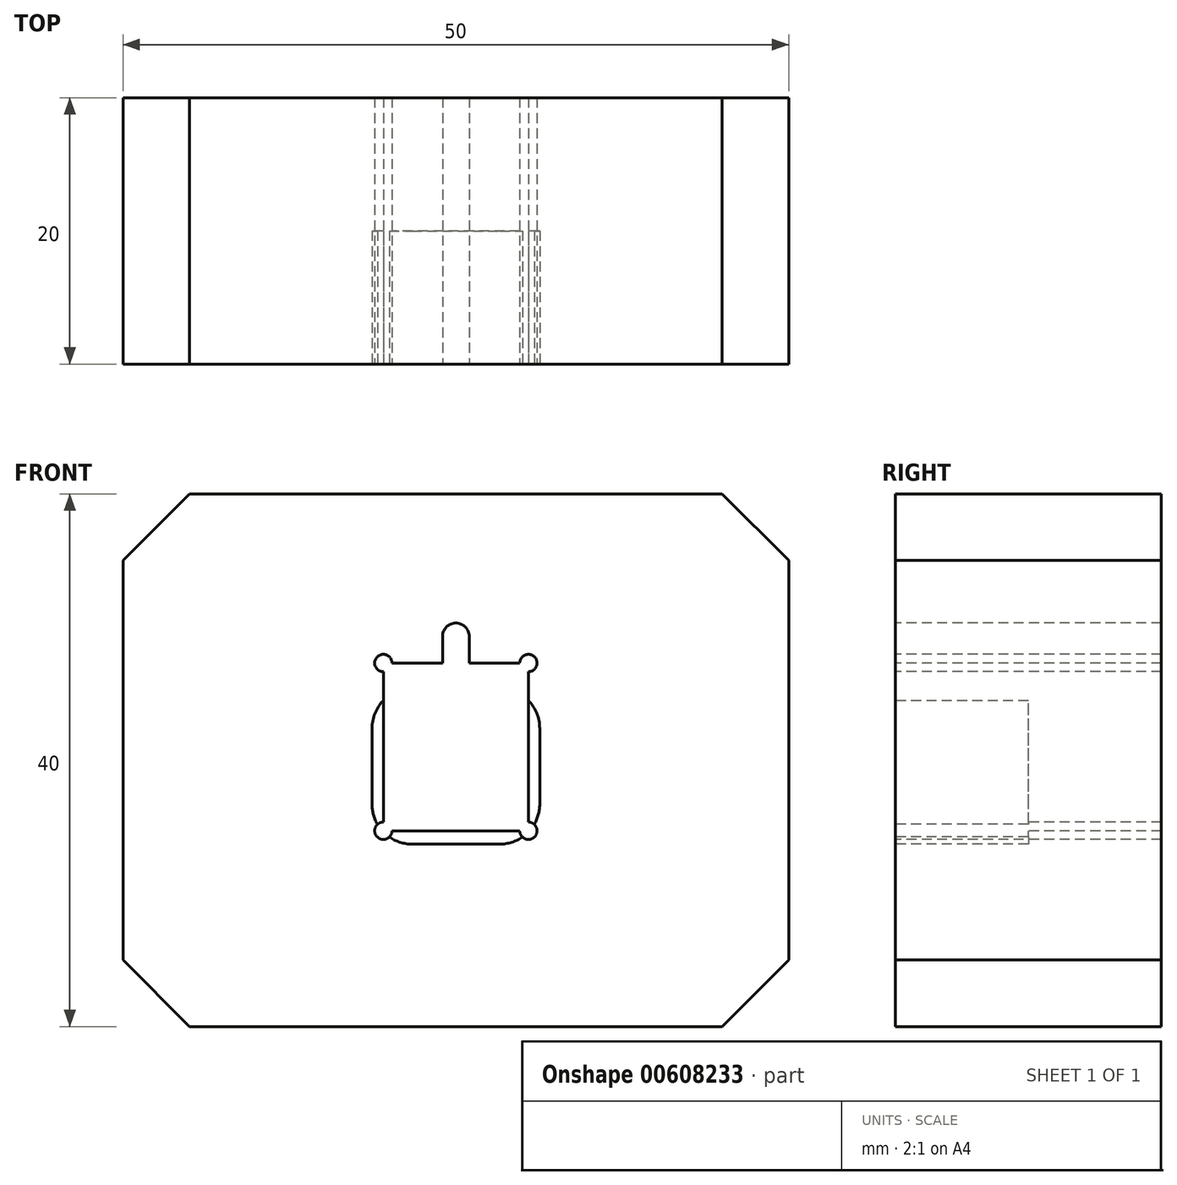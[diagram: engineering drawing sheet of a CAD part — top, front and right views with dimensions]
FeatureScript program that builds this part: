
annotation { "Feature Type Name" : "Feature", "Feature Type Description" : "" }
export const myFeature = defineFeature(function(context is Context, id is Id, definition is map)
    precondition{}
    {
        {
            var Q0;
            Q0=qCreatedBy(makeId("Front.planeOp"),FACE);
            var sketch = newSketch(context, id + "F0", { "sketchPlane" : qUnion([Q0])});
            skLineSegment(sketch, "E0.bottom", {"start": v(-25, 20) * mm, "end": v(25, 20) * mm});
            skLineSegment(sketch, "E0.top", {"start": v(-25, -20) * mm, "end": v(25, -20) * mm});
            skLineSegment(sketch, "E0.left", {"start": v(-25, 20) * mm, "end": v(-25, -20) * mm});
            skLineSegment(sketch, "E0.right", {"start": v(25, 20) * mm, "end": v(25, -20) * mm});
            skPoint(sketch, "E0.middle", {"position": v(0, 0) * mm});
            skSolve(sketch);
        }
        {
            var Q0;
            Q0 = qSketchRegion(id + "F0", true);
            extrude(context, id + "F1", {"entities" : qUnion([Q0]), "depth" : 20 * mm, "offsetDistance" : 25 * mm});
        }
        {
            var Q0;
            Q0=makeQuery(id+"F1.opExtrude","SWEPT_EDGE",EDGE,{"disambiguationData":[OSD([sQuery(id+"F0.wireOp",EDGE,"E0.bottom"),sQuery(id+"F0.wireOp",EDGE,"E0.left")])]});
            var Q1;
            Q1=makeQuery(id+"F1.opExtrude","SWEPT_EDGE",EDGE,{"disambiguationData":[OSD([sQuery(id+"F0.wireOp",EDGE,"E0.bottom"),sQuery(id+"F0.wireOp",EDGE,"E0.right")])]});
            var Q2;
            Q2=makeQuery(id+"F1.opExtrude","SWEPT_EDGE",EDGE,{"disambiguationData":[OSD([sQuery(id+"F0.wireOp",EDGE,"E0.top"),sQuery(id+"F0.wireOp",EDGE,"E0.left")])]});
            var Q3;
            Q3=makeQuery(id+"F1.opExtrude","SWEPT_EDGE",EDGE,{"disambiguationData":[OSD([sQuery(id+"F0.wireOp",EDGE,"E0.top"),sQuery(id+"F0.wireOp",EDGE,"E0.right")])]});
            chamfer(context, id + "F2", {"entities" : qUnion([Q0, Q1, Q2, Q3]), "width" : 5 * mm, "tangentPropagation" : true});
        }
        {
            var Q0;
            Q0=makeQuery(id+"F1.opExtrude","CAP_FACE",FACE,{"disambiguationData":[OSD([sQuery(id+"F0.wireOp",EDGE,"E0.bottom"),sQuery(id+"F0.wireOp",EDGE,"E0.top"),sQuery(id+"F0.wireOp",EDGE,"E0.left"),sQuery(id+"F0.wireOp",EDGE,"E0.right")])],"isStart":false});
            var sketch = newSketch(context, id + "F3", { "sketchPlane" : qUnion([Q0])});
            skLineSegment(sketch, "E1.bottom", {"start": v(-4.8, 7.3) * mm, "end": v(-1, 7.3) * mm});
            skLineSegment(sketch, "E1.top", {"start": v(-4.8, -5.3) * mm, "end": v(4.8, -5.3) * mm});
            skLineSegment(sketch, "E1.left", {"start": v(-5.45, 6.65) * mm, "end": v(-5.45, -4.65) * mm});
            skLineSegment(sketch, "E1.right", {"start": v(5.45, 6.65) * mm, "end": v(5.45, -4.65) * mm});
            skLineSegment(sketch, "E2.bottom", {"start": v(0, 10.3) * mm, "end": v(0, 10.3) * mm});
            skLineSegment(sketch, "E2.left", {"start": v(-1, 9.3) * mm, "end": v(-1, 7.3) * mm});
            skLineSegment(sketch, "E2.right", {"start": v(1, 9.3) * mm, "end": v(1, 7.3) * mm});
            skArc(sketch, "E3.filletArc", {"start": v(0, 10.3) * mm, "mid": v(-0.7, 10) * mm, "end": v(-1, 9.3) * mm});
            skArc(sketch, "E4.filletArc", {"start": v(1, 9.3) * mm, "mid": v(0.7, 10) * mm, "end": v(0, 10.3) * mm});
            skArc(sketch, "E5", {"start": v(-4.8, 7.3) * mm, "mid": v(-5.9, 7.76) * mm, "end": v(-5.45, 6.65) * mm});
            skArc(sketch, "E6", {"start": v(4.8, -5.3) * mm, "mid": v(5.9, -5.76) * mm, "end": v(5.45, -4.65) * mm});
            skLineSegment(sketch, "E7.trimOffspring", {"start": v(1, 7.3) * mm, "end": v(4.8, 7.3) * mm});
            skArc(sketch, "E8.MirrorCS", {"start": v(4.8, 7.3) * mm, "mid": v(5.9, 7.76) * mm, "end": v(5.45, 6.65) * mm});
            skArc(sketch, "E9.MirrorCS", {"start": v(-4.8, -5.3) * mm, "mid": v(-5.9, -5.76) * mm, "end": v(-5.45, -4.65) * mm});
            skSolve(sketch);
        }
        {
            var Q0;
            Q0 = qSketchRegion(id + "F3", true);
            extrude(context, id + "F4", {"entities" : qUnion([Q0]), "operationType" : NewBodyOperationType.REMOVE, "oppositeDirection" : true, "depth" : 20 * mm, "offsetDistance" : 25 * mm});
        }
        {
            var Q0;
            Q0=makeQuery(id+"F1.opExtrude","CAP_FACE",FACE,{"disambiguationData":[OSD([sQuery(id+"F0.wireOp",EDGE,"E0.bottom"),sQuery(id+"F0.wireOp",EDGE,"E0.top"),sQuery(id+"F0.wireOp",EDGE,"E0.left"),sQuery(id+"F0.wireOp",EDGE,"E0.right")])],"isStart":false});
            var sketch = newSketch(context, id + "F5", { "sketchPlane" : qUnion([Q0])});
            skLineSegment(sketch, "E10.bottom", {"start": v(-3.3, -6.3) * mm, "end": v(3.3, -6.3) * mm});
            skLineSegment(sketch, "E10.top", {"start": v(-3.3, 5.4) * mm, "end": v(3.3, 5.4) * mm});
            skLineSegment(sketch, "E10.left", {"start": v(-6.3, -3.3) * mm, "end": v(-6.3, 2.4) * mm});
            skLineSegment(sketch, "E10.right", {"start": v(6.3, -3.3) * mm, "end": v(6.3, 2.4) * mm});
            skPoint(sketch, "E11.visualSharp", {"position": v(-6.3, -6.3) * mm});
            skArc(sketch, "E11.filletArc", {"start": v(-6.3, -3.3) * mm, "mid": v(-5.42, -5.42) * mm, "end": v(-3.3, -6.3) * mm});
            skPoint(sketch, "E12.visualSharp", {"position": v(6.3, -6.3) * mm});
            skArc(sketch, "E12.filletArc", {"start": v(3.3, -6.3) * mm, "mid": v(5.42, -5.42) * mm, "end": v(6.3, -3.3) * mm});
            skPoint(sketch, "E13.visualSharp", {"position": v(6.3, 5.4) * mm});
            skArc(sketch, "E13.filletArc", {"start": v(6.3, 2.4) * mm, "mid": v(5.42, 4.51) * mm, "end": v(3.3, 5.4) * mm});
            skPoint(sketch, "E14.visualSharp", {"position": v(-6.3, 5.4) * mm});
            skArc(sketch, "E14.filletArc", {"start": v(-3.3, 5.4) * mm, "mid": v(-5.42, 4.51) * mm, "end": v(-6.3, 2.4) * mm});
            skSolve(sketch);
        }
        {
            var Q0;
            Q0 = qSketchRegion(id + "F5", true);
            extrude(context, id + "F6", {"entities" : qUnion([Q0]), "operationType" : NewBodyOperationType.REMOVE, "oppositeDirection" : true, "depth" : 10 * mm, "offsetDistance" : 25 * mm});
        }
    });
